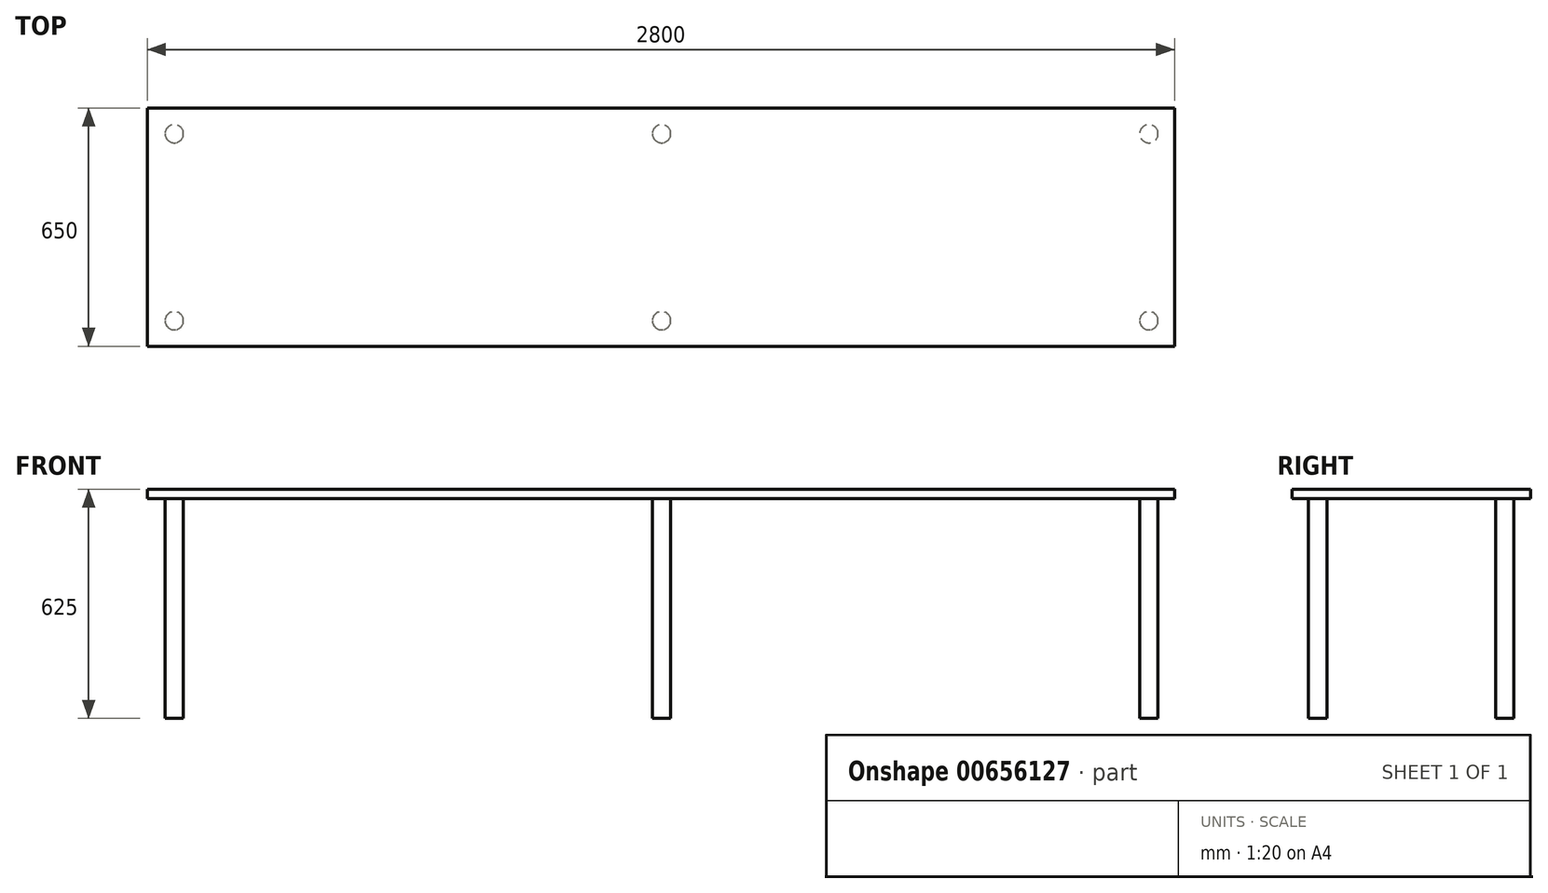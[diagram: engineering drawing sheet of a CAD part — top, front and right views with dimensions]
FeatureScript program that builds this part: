
annotation { "Feature Type Name" : "Feature", "Feature Type Description" : "" }
export const myFeature = defineFeature(function(context is Context, id is Id, definition is map)
    precondition{}
    {
        {
            var Q0;
            Q0=qCreatedBy(makeId("Front.planeOp"),FACE);
            var sketch = newSketch(context, id + "F0", { "sketchPlane" : qUnion([Q0])});
            skLineSegment(sketch, "E0.bottom", {"start": v(0, 0) * mm, "end": v(2800, 0) * mm});
            skLineSegment(sketch, "E0.top", {"start": v(0, -25) * mm, "end": v(2800, -25) * mm});
            skLineSegment(sketch, "E0.left", {"start": v(0, 0) * mm, "end": v(0, -25) * mm});
            skLineSegment(sketch, "E0.right", {"start": v(2800, 0) * mm, "end": v(2800, -25) * mm});
            skSolve(sketch);
        }
        {
            var Q0;
            Q0=makeQuery(id+"F0.imprint","IMPRINT",FACE,{"disambiguationData":[TD([[makeQuery(id+"F0.imprint","IMPRINT",EDGE,{"derivedFrom":sQuery(id+"F0.wireOp",EDGE,"E0.bottom")}),-1.0]])]});
            extrude(context, id + "F1", {"entities" : qUnion([Q0]), "depth" : 650 * mm, "offsetDistance" : 25.4 * mm});
        }
        {
            var Q0;
            Q0=makeQuery(id+"F1.opExtrude","SWEPT_FACE",FACE,{"disambiguationData":[OSD([sQuery(id+"F0.wireOp",EDGE,"E0.top")])]});
            var sketch = newSketch(context, id + "F2", { "sketchPlane" : qUnion([Q0])});
            skCircle(sketch, "E1", {"center": v(2730, 70) * mm, "radius": 25 * mm});
            skCircle(sketch, "E2.0.1.0", {"center": v(2730, 580) * mm, "radius": 25 * mm});
            skCircle(sketch, "E2.1.0.0", {"center": v(1401.58, 70) * mm, "radius": 25 * mm});
            skCircle(sketch, "E2.1.1.0", {"center": v(1401.58, 580) * mm, "radius": 25 * mm});
            skCircle(sketch, "E2.2.0.0", {"center": v(73.16, 70) * mm, "radius": 25 * mm});
            skCircle(sketch, "E2.2.1.0", {"center": v(73.16, 580) * mm, "radius": 25 * mm});
            skLineSegment(sketch, "E2.direction1", {"start": v(2730, 70) * mm, "end": v(1401.58, 70) * mm, "construction": true});
            skLineSegment(sketch, "E2.direction2", {"start": v(2730, 70) * mm, "end": v(2730, 580) * mm, "construction": true});
            skSolve(sketch);
        }
        {
            var Q0;
            Q0=makeQuery(id+"F2.imprint","IMPRINT",FACE,{"disambiguationData":[TD([[makeQuery(id+"F2.imprint","IMPRINT",EDGE,{"derivedFrom":sQuery(id+"F2.wireOp",EDGE,"E2.2.0.0")}),1.0]])]});
            var Q1;
            Q1=makeQuery(id+"F2.imprint","IMPRINT",FACE,{"disambiguationData":[TD([[makeQuery(id+"F2.imprint","IMPRINT",EDGE,{"derivedFrom":sQuery(id+"F2.wireOp",EDGE,"E2.2.1.0")}),1.0]])]});
            var Q2;
            Q2=makeQuery(id+"F2.imprint","IMPRINT",FACE,{"disambiguationData":[TD([[makeQuery(id+"F2.imprint","IMPRINT",EDGE,{"derivedFrom":sQuery(id+"F2.wireOp",EDGE,"E2.1.0.0")}),1.0]])]});
            var Q3;
            Q3=makeQuery(id+"F2.imprint","IMPRINT",FACE,{"disambiguationData":[TD([[makeQuery(id+"F2.imprint","IMPRINT",EDGE,{"derivedFrom":sQuery(id+"F2.wireOp",EDGE,"E2.1.1.0")}),1.0]])]});
            var Q4;
            Q4=makeQuery(id+"F2.imprint","IMPRINT",FACE,{"disambiguationData":[TD([[makeQuery(id+"F2.imprint","IMPRINT",EDGE,{"derivedFrom":sQuery(id+"F2.wireOp",EDGE,"E1")}),1.0]])]});
            var Q5;
            Q5=makeQuery(id+"F2.imprint","IMPRINT",FACE,{"disambiguationData":[TD([[makeQuery(id+"F2.imprint","IMPRINT",EDGE,{"derivedFrom":sQuery(id+"F2.wireOp",EDGE,"E2.0.1.0")}),1.0]])]});
            extrude(context, id + "F3", {"entities" : qUnion([Q0, Q1, Q2, Q3, Q4, Q5]), "operationType" : NewBodyOperationType.ADD, "depth" : 600 * mm, "offsetDistance" : 25.4 * mm});
        }
    });
